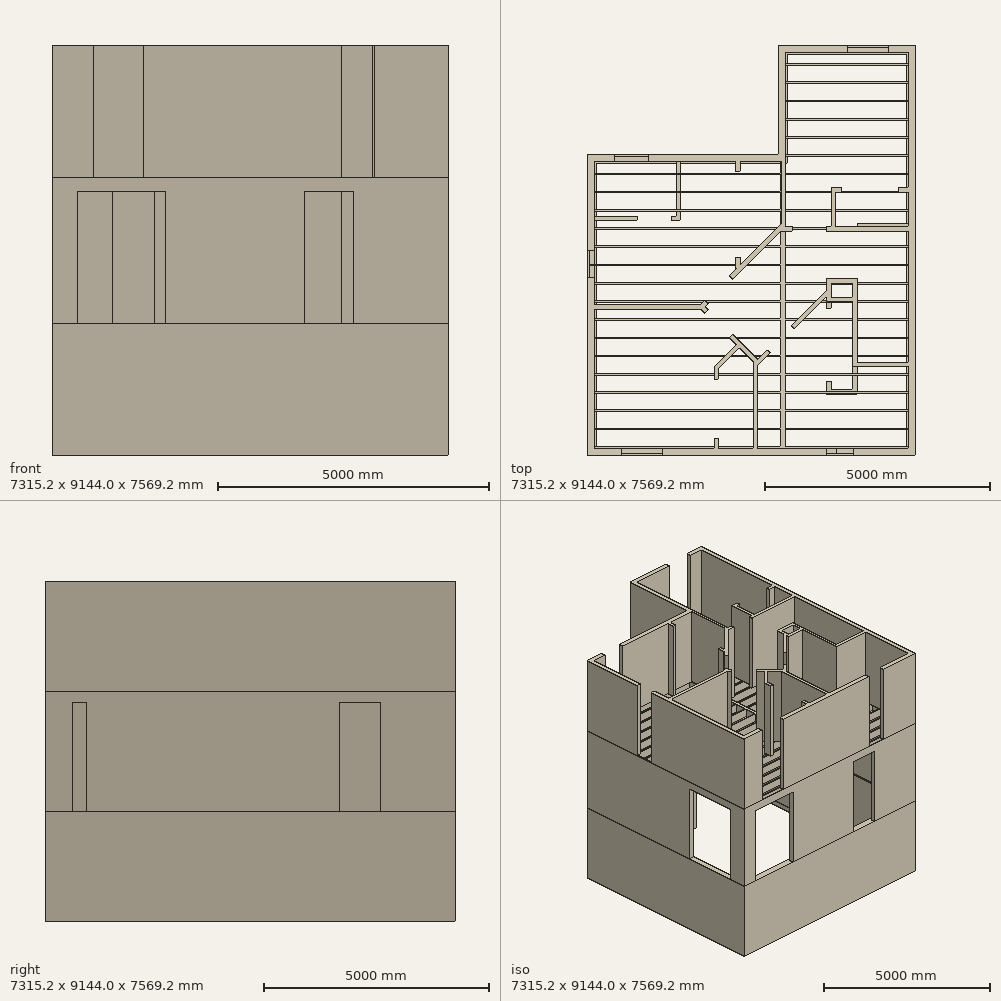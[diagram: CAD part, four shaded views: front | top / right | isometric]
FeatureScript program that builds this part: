
annotation { "Feature Type Name" : "Feature", "Feature Type Description" : "" }
export const myFeature = defineFeature(function(context is Context, id is Id, definition is map)
    precondition{}
    {
        {
            var Q0;
            Q0=qCreatedBy(makeId("Top.planeOp"),FACE);
            cPlane(context, id + "F0", {"entities" : qUnion([Q0]), "cplaneType" : CPlaneType.OFFSET, "offset" : 2692.4 * mm, "width" : 152.4 * mm, "height" : 152.4 * mm});
        }
        {
            var Q0;
            Q0=qCreatedBy(makeId("Top.planeOp"),FACE);
            var sketch = newSketch(context, id + "F1", { "sketchPlane" : qUnion([Q0])});
            skLineSegment(sketch, "E0", {"start": v(-4267.2, 6705.6) * mm, "end": v(0, 6705.6) * mm});
            skLineSegment(sketch, "E1", {"start": v(0, 9144) * mm, "end": v(0, 6705.6) * mm});
            skLineSegment(sketch, "E2", {"start": v(0, 9144) * mm, "end": v(3048, 9144) * mm});
            skLineSegment(sketch, "E3", {"start": v(3048, 9144) * mm, "end": v(3048, 0) * mm});
            skLineSegment(sketch, "E4", {"start": v(3048, 0) * mm, "end": v(-4267.2, 0) * mm});
            skLineSegment(sketch, "E5", {"start": v(-4267.2, 0) * mm, "end": v(-4267.2, 6705.6) * mm});
            skLineSegment(sketch, "E6", {"start": v(-4267.2, 6705.6) * mm, "end": v(-4267.2, 10363.2) * mm});
            skLineSegment(sketch, "E7", {"start": v(-3048, 11582.4) * mm, "end": v(3048, 11582.4) * mm});
            skLineSegment(sketch, "E8", {"start": v(3048, 11582.4) * mm, "end": v(3048, 9144) * mm});
            skLineSegment(sketch, "E9", {"start": v(-4267.2, 0) * mm, "end": v(-4267.2, -2743.2) * mm});
            skLineSegment(sketch, "E10", {"start": v(-4267.2, -2743.2) * mm, "end": v(3048, -2743.2) * mm});
            skLineSegment(sketch, "E11", {"start": v(3048, -2743.2) * mm, "end": v(3048, 0) * mm});
            skLineSegment(sketch, "E12", {"start": v(-4267.2, 10363.2) * mm, "end": v(-3048, 11582.4) * mm});
            skSolve(sketch);
        }
        {
            var Q0;
            Q0=qCreatedBy(makeId("Top.planeOp"),FACE);
            var sketch = newSketch(context, id + "F2", { "sketchPlane" : qUnion([Q0])});
            skLineSegment(sketch, "E13", {"start": v(0, 0) * mm, "end": v(-4267.2, 0) * mm});
            skLineSegment(sketch, "E14", {"start": v(-4267.2, 0) * mm, "end": v(-4267.2, 6705.6) * mm});
            skLineSegment(sketch, "E15", {"start": v(-4267.2, 6705.6) * mm, "end": v(0, 6705.6) * mm});
            skLineSegment(sketch, "E16", {"start": v(0, 6705.6) * mm, "end": v(0, 9144) * mm});
            skLineSegment(sketch, "E17", {"start": v(0, 9144) * mm, "end": v(3048, 9144) * mm});
            skLineSegment(sketch, "E18", {"start": v(3048, 9144) * mm, "end": v(3048, 0) * mm});
            skLineSegment(sketch, "E19", {"start": v(3048, 0) * mm, "end": v(0, 0) * mm});
            skLineSegment(sketch, "E20.0", {"start": v(203.2, 6502.4) * mm, "end": v(203.2, 8940.8) * mm});
            skLineSegment(sketch, "E20.1", {"start": v(-4064, 6502.4) * mm, "end": v(203.2, 6502.4) * mm});
            skLineSegment(sketch, "E20.2", {"start": v(2844.8, 8940.8) * mm, "end": v(2844.8, 203.2) * mm});
            skLineSegment(sketch, "E20.3", {"start": v(2844.8, 203.2) * mm, "end": v(0, 203.2) * mm});
            skLineSegment(sketch, "E20.4", {"start": v(0, 203.2) * mm, "end": v(-4064, 203.2) * mm});
            skLineSegment(sketch, "E20.5", {"start": v(203.2, 8940.8) * mm, "end": v(2844.8, 8940.8) * mm});
            skLineSegment(sketch, "E20.6", {"start": v(-4064, 203.2) * mm, "end": v(-4064, 6502.4) * mm});
            skSolve(sketch);
        }
        {
            var Q0;
            Q0 = qSketchRegion(id + "F2", true);
            extrude(context, id + "F3", {"entities" : qUnion([Q0]), "oppositeDirection" : true, "depth" : 2438.4 * mm});
        }
        {
            var Q0;
            Q0=makeQuery(id+"F1.imprint","IMPRINT",FACE,{"disambiguationData":[TD([[makeQuery(id+"F1.imprint","IMPRINT",EDGE,{"derivedFrom":sQuery(id+"F1.wireOp",EDGE,"E0")}),1.0]])]});
            var sketch = newSketch(context, id + "F4", { "sketchPlane" : qUnion([Q0])});
            skLineSegment(sketch, "E21.bottom", {"start": v(-4267.2, 0) * mm, "end": v(-3810, 0) * mm});
            skLineSegment(sketch, "E21.top", {"start": v(-4114.8, 152.4) * mm, "end": v(-3810, 152.4) * mm});
            skLineSegment(sketch, "E21.left", {"start": v(-4267.2, 0) * mm, "end": v(-4267.2, 152.4) * mm});
            skLineSegment(sketch, "E21.right", {"start": v(-3810, 0) * mm, "end": v(-3810, 152.4) * mm});
            skLineSegment(sketch, "E22.top", {"start": v(-4267.2, 609.6) * mm, "end": v(-4114.8, 609.6) * mm});
            skLineSegment(sketch, "E22.left", {"start": v(-4267.2, 152.4) * mm, "end": v(-4267.2, 609.6) * mm});
            skLineSegment(sketch, "E22.right", {"start": v(-4114.8, 152.4) * mm, "end": v(-4114.8, 609.6) * mm});
            skLineSegment(sketch, "E23.bottom", {"start": v(-4267.2, 2336.8) * mm, "end": v(-4114.8, 2336.8) * mm});
            skLineSegment(sketch, "E23.top", {"start": v(-4267.2, 6705.6) * mm, "end": v(-4114.8, 6705.6) * mm});
            skLineSegment(sketch, "E23.left", {"start": v(-4267.2, 2336.8) * mm, "end": v(-4267.2, 6705.6) * mm});
            skLineSegment(sketch, "E23.right", {"start": v(-4114.8, 2336.8) * mm, "end": v(-4114.8, 5232.4) * mm});
            skLineSegment(sketch, "E24.bottom", {"start": v(-4114.8, 6705.6) * mm, "end": v(-1879.6, 6705.6) * mm});
            skLineSegment(sketch, "E24.top", {"start": v(-4114.8, 6553.2) * mm, "end": v(-2286, 6553.2) * mm});
            skLineSegment(sketch, "E24.right", {"start": v(-1879.6, 6705.6) * mm, "end": v(-1879.6, 6553.2) * mm});
            skLineSegment(sketch, "E25.bottom", {"start": v(-1066.8, 6705.6) * mm, "end": v(0, 6705.6) * mm});
            skLineSegment(sketch, "E25.top", {"start": v(-1066.8, 6553.2) * mm, "end": v(0, 6553.2) * mm});
            skLineSegment(sketch, "E25.left", {"start": v(-1066.8, 6705.6) * mm, "end": v(-1066.8, 6553.2) * mm});
            skLineSegment(sketch, "E26.bottom", {"start": v(0, 6553.2) * mm, "end": v(152.4, 6553.2) * mm});
            skLineSegment(sketch, "E26.top", {"start": v(0, 9144) * mm, "end": v(152.4, 9144) * mm});
            skLineSegment(sketch, "E26.left", {"start": v(0, 6705.6) * mm, "end": v(0, 9144) * mm});
            skLineSegment(sketch, "E26.right", {"start": v(152.4, 6553.2) * mm, "end": v(152.4, 8991.6) * mm});
            skLineSegment(sketch, "E27.bottom", {"start": v(152.4, 9144) * mm, "end": v(3048, 9144) * mm});
            skLineSegment(sketch, "E27.top", {"start": v(152.4, 8991.6) * mm, "end": v(2895.6, 8991.6) * mm});
            skLineSegment(sketch, "E28.top", {"start": v(3048, 7467.6) * mm, "end": v(2895.6, 7467.6) * mm});
            skLineSegment(sketch, "E28.left", {"start": v(3048, 8991.6) * mm, "end": v(3048, 7467.6) * mm});
            skLineSegment(sketch, "E28.right", {"start": v(2895.6, 8991.6) * mm, "end": v(2895.6, 7467.6) * mm});
            skLineSegment(sketch, "E29.bottom", {"start": v(3048, 6553.2) * mm, "end": v(2895.6, 6553.2) * mm});
            skLineSegment(sketch, "E29.top", {"start": v(3048, 914.4) * mm, "end": v(2895.6, 914.4) * mm});
            skLineSegment(sketch, "E29.left", {"start": v(3048, 6553.2) * mm, "end": v(3048, 914.4) * mm});
            skLineSegment(sketch, "E29.right", {"start": v(2895.6, 6553.2) * mm, "end": v(2895.6, 5181.6) * mm});
            skLineSegment(sketch, "E30.bottom", {"start": v(-2184.4, 0) * mm, "end": v(381, 0) * mm});
            skLineSegment(sketch, "E30.top", {"start": v(-2184.4, 152.4) * mm, "end": v(50.8, 152.4) * mm});
            skLineSegment(sketch, "E30.left", {"start": v(-2184.4, 0) * mm, "end": v(-2184.4, 152.4) * mm});
            skLineSegment(sketch, "E31.bottom", {"start": v(1295.4, 152.4) * mm, "end": v(2895.6, 152.4) * mm});
            skLineSegment(sketch, "E31.top", {"start": v(1295.4, 0) * mm, "end": v(3048, 0) * mm});
            skLineSegment(sketch, "E31.left", {"start": v(1295.4, 152.4) * mm, "end": v(1295.4, 0) * mm});
            skLineSegment(sketch, "E31.right", {"start": v(3048, 152.4) * mm, "end": v(3048, 0) * mm});
            skLineSegment(sketch, "E32.top", {"start": v(3048, 609.6) * mm, "end": v(2895.6, 609.6) * mm});
            skLineSegment(sketch, "E32.left", {"start": v(3048, 152.4) * mm, "end": v(3048, 609.6) * mm});
            skLineSegment(sketch, "E32.right", {"start": v(2895.6, 152.4) * mm, "end": v(2895.6, 609.6) * mm});
            skLineSegment(sketch, "E33.bottom", {"start": v(-4114.8, 5334) * mm, "end": v(-3149.6, 5334) * mm});
            skLineSegment(sketch, "E33.top", {"start": v(-4114.8, 5232.4) * mm, "end": v(-3149.6, 5232.4) * mm});
            skLineSegment(sketch, "E33.right", {"start": v(-3149.6, 5334) * mm, "end": v(-3149.6, 5232.4) * mm});
            skLineSegment(sketch, "E34.bottom", {"start": v(-2387.6, 5334) * mm, "end": v(-2286, 5334) * mm});
            skLineSegment(sketch, "E34.top", {"start": v(-2387.6, 5232.4) * mm, "end": v(-2184.4, 5232.4) * mm});
            skLineSegment(sketch, "E34.left", {"start": v(-2387.6, 5334) * mm, "end": v(-2387.6, 5232.4) * mm});
            skLineSegment(sketch, "E34.right", {"start": v(-2184.4, 5334) * mm, "end": v(-2184.4, 5232.4) * mm});
            skLineSegment(sketch, "E35.left", {"start": v(-2184.4, 5334) * mm, "end": v(-2184.4, 6553.2) * mm});
            skLineSegment(sketch, "E35.right", {"start": v(-2286, 5334) * mm, "end": v(-2286, 6553.2) * mm});
            skLineSegment(sketch, "E36.bottom", {"start": v(381, 152.4) * mm, "end": v(152.4, 152.4) * mm});
            skLineSegment(sketch, "E36.top", {"start": v(152.4, 1066.8) * mm, "end": v(50.8, 1066.8) * mm});
            skLineSegment(sketch, "E36.left", {"start": v(152.4, 152.4) * mm, "end": v(152.4, 1066.8) * mm});
            skLineSegment(sketch, "E36.right", {"start": v(50.8, 152.4) * mm, "end": v(50.8, 1066.8) * mm});
            skLineSegment(sketch, "E37.bottom", {"start": v(50.8, 3937.1) * mm, "end": v(152.4, 3937.1) * mm});
            skLineSegment(sketch, "E37.top", {"start": v(50.8, 2286) * mm, "end": v(152.4, 2286) * mm});
            skLineSegment(sketch, "E37.left", {"start": v(50.8, 3937.1) * mm, "end": v(50.8, 2286) * mm});
            skLineSegment(sketch, "E37.right", {"start": v(152.4, 3937.1) * mm, "end": v(152.4, 2286) * mm});
            skLineSegment(sketch, "E38", {"start": v(1066.8, 3937.1) * mm, "end": v(1752.6, 3937.1) * mm});
            skLineSegment(sketch, "E39", {"start": v(1752.6, 3937.1) * mm, "end": v(1752.6, 1371.6) * mm});
            skLineSegment(sketch, "E40", {"start": v(1752.6, 1371.6) * mm, "end": v(1066.8, 1371.6) * mm});
            skLineSegment(sketch, "E41", {"start": v(1066.8, 1371.6) * mm, "end": v(1066.8, 1655.98) * mm});
            skLineSegment(sketch, "E42", {"start": v(1066.8, 3937.1) * mm, "end": v(1066.8, 3276.8) * mm});
            skLineSegment(sketch, "E43.0", {"start": v(1168.4, 3835.5) * mm, "end": v(1168.4, 3530.7) * mm});
            skLineSegment(sketch, "E43.1", {"start": v(1168.4, 1473.2) * mm, "end": v(1168.4, 1655.98) * mm});
            skLineSegment(sketch, "E43.2", {"start": v(1651, 1473.2) * mm, "end": v(1168.4, 1473.2) * mm});
            skLineSegment(sketch, "E43.3", {"start": v(1651, 3835.5) * mm, "end": v(1651, 3530.7) * mm});
            skLineSegment(sketch, "E43.4", {"start": v(1168.4, 3835.5) * mm, "end": v(1651, 3835.5) * mm});
            skLineSegment(sketch, "E44", {"start": v(1066.8, 1655.98) * mm, "end": v(1168.4, 1655.98) * mm});
            skLineSegment(sketch, "E45", {"start": v(1066.8, 3276.8) * mm, "end": v(1168.4, 3276.8) * mm});
            skLineSegment(sketch, "E46", {"start": v(1168.4, 3429.2) * mm, "end": v(1651, 3429.2) * mm});
            skLineSegment(sketch, "E47", {"start": v(1651, 3530.7) * mm, "end": v(1168.4, 3530.7) * mm});
            skLineSegment(sketch, "E48.trimOffspring", {"start": v(1168.4, 3429.2) * mm, "end": v(1168.4, 3276.8) * mm});
            skLineSegment(sketch, "E49.trimOffspring", {"start": v(1651, 3429.2) * mm, "end": v(1651, 1473.2) * mm});
            skPoint(sketch, "E50.orphan", {"position": v(152.4, 152.4) * mm});
            skLineSegment(sketch, "E51", {"start": v(381, 152.4) * mm, "end": v(381, 0) * mm});
            skLineSegment(sketch, "E52.trimOffspring", {"start": v(-2184.4, 6553.2) * mm, "end": v(-1879.6, 6553.2) * mm});
            skLineSegment(sketch, "E53.trimOffspring", {"start": v(-4114.8, 5334) * mm, "end": v(-4114.8, 6553.2) * mm});
            skLineSegment(sketch, "E54", {"start": v(3048, 9144) * mm, "end": v(3048, 8991.6) * mm});
            skLineSegment(sketch, "E55", {"start": v(2895.6, 5181.6) * mm, "end": v(1752.6, 5181.6) * mm});
            skLineSegment(sketch, "E56", {"start": v(1752.6, 5181.6) * mm, "end": v(1752.6, 5080.1) * mm});
            skLineSegment(sketch, "E57", {"start": v(1752.6, 5080.1) * mm, "end": v(2895.6, 5080.1) * mm});
            skLineSegment(sketch, "E58.trimOffspring", {"start": v(2895.6, 5080.1) * mm, "end": v(2895.6, 914.4) * mm});
            skSolve(sketch);
        }
        {
            var Q0;
            Q0 = qSketchRegion(id + "F4", true);
            extrude(context, id + "F5", {"entities" : qUnion([Q0]), "depth" : 2438.4 * mm});
        }
        {
            var Q0;
            Q0=qCreatedBy(makeId("Front.planeOp"),FACE);
            var sketch = newSketch(context, id + "F6", { "sketchPlane" : qUnion([Q0])});
            skLineSegment(sketch, "E59.bottom", {"start": v(152.4, 2692.4) * mm, "end": v(38.1, 2692.4) * mm});
            skLineSegment(sketch, "E59.top", {"start": v(152.4, 2438.4) * mm, "end": v(38.1, 2438.4) * mm});
            skLineSegment(sketch, "E59.left", {"start": v(152.4, 2692.4) * mm, "end": v(152.4, 2438.4) * mm});
            skLineSegment(sketch, "E59.right", {"start": v(38.1, 2692.4) * mm, "end": v(38.1, 2438.4) * mm});
            skPoint(sketch, "E60.firstSnap0", {"position": v(95.25, 2692.4) * mm});
            skLineSegment(sketch, "E60.bottom", {"start": v(3048, 2692.4) * mm, "end": v(3009.9, 2692.4) * mm});
            skLineSegment(sketch, "E60.top", {"start": v(3048, 2438.4) * mm, "end": v(3009.9, 2438.4) * mm});
            skLineSegment(sketch, "E60.left", {"start": v(3048, 2692.4) * mm, "end": v(3048, 2438.4) * mm});
            skLineSegment(sketch, "E60.right", {"start": v(3009.9, 2692.4) * mm, "end": v(3009.9, 2438.4) * mm});
            skLineSegment(sketch, "E61.bottom", {"start": v(-4229.1, 2692.4) * mm, "end": v(-4267.2, 2692.4) * mm});
            skLineSegment(sketch, "E61.top", {"start": v(-4229.1, 2438.4) * mm, "end": v(-4267.2, 2438.4) * mm});
            skLineSegment(sketch, "E61.left", {"start": v(-4229.1, 2692.4) * mm, "end": v(-4229.1, 2438.4) * mm});
            skLineSegment(sketch, "E61.right", {"start": v(-4267.2, 2692.4) * mm, "end": v(-4267.2, 2438.4) * mm});
            skSolve(sketch);
        }
        {
            var Q0;
            Q0 = qSketchRegion(id + "F6", true);
            var Q1;
            Q1=makeQuery(id+"F5.opExtrude","SWEPT_FACE",FACE,{"disambiguationData":[OSD([sQuery(id+"F4.wireOp",EDGE,"E26.top"),sQuery(id+"F4.wireOp",EDGE,"E27.bottom")])]});
            extrude(context, id + "F7", {"entities" : qUnion([Q0]), "oppositeDirection" : true, "depth" : 9144 * mm});
        }
        {
            var Q0;
            Q0=makeQuery(id+"F5.opExtrude","SWEPT_FACE",FACE,{"disambiguationData":[OSD([sQuery(id+"F4.wireOp",EDGE,"E23.left")])]});
            var sketch = newSketch(context, id + "F8", { "sketchPlane" : qUnion([Q0])});
            skLineSegment(sketch, "E62.bottom", {"start": v(-9144, 2692.4) * mm, "end": v(-9105.9, 2692.4) * mm});
            skLineSegment(sketch, "E62.top", {"start": v(-9144, 2438.4) * mm, "end": v(-9105.9, 2438.4) * mm});
            skLineSegment(sketch, "E62.left", {"start": v(-9144, 2692.4) * mm, "end": v(-9144, 2438.4) * mm});
            skLineSegment(sketch, "E62.right", {"start": v(-9105.9, 2692.4) * mm, "end": v(-9105.9, 2438.4) * mm});
            skLineSegment(sketch, "E63.1.0.0", {"start": v(-8737.6, 2438.4) * mm, "end": v(-8699.5, 2438.4) * mm});
            skLineSegment(sketch, "E63.1.0.1", {"start": v(-8737.6, 2692.4) * mm, "end": v(-8737.6, 2438.4) * mm});
            skLineSegment(sketch, "E63.1.0.2", {"start": v(-8699.5, 2692.4) * mm, "end": v(-8699.5, 2438.4) * mm});
            skLineSegment(sketch, "E63.1.0.3", {"start": v(-8737.6, 2692.4) * mm, "end": v(-8699.5, 2692.4) * mm});
            skLineSegment(sketch, "E63.2.0.0", {"start": v(-8331.2, 2438.4) * mm, "end": v(-8293.1, 2438.4) * mm});
            skLineSegment(sketch, "E63.2.0.1", {"start": v(-8331.2, 2692.4) * mm, "end": v(-8331.2, 2438.4) * mm});
            skLineSegment(sketch, "E63.2.0.2", {"start": v(-8293.1, 2692.4) * mm, "end": v(-8293.1, 2438.4) * mm});
            skLineSegment(sketch, "E63.2.0.3", {"start": v(-8331.2, 2692.4) * mm, "end": v(-8293.1, 2692.4) * mm});
            skLineSegment(sketch, "E63.3.0.0", {"start": v(-7924.8, 2438.4) * mm, "end": v(-7886.7, 2438.4) * mm});
            skLineSegment(sketch, "E63.3.0.1", {"start": v(-7924.8, 2692.4) * mm, "end": v(-7924.8, 2438.4) * mm});
            skLineSegment(sketch, "E63.3.0.2", {"start": v(-7886.7, 2692.4) * mm, "end": v(-7886.7, 2438.4) * mm});
            skLineSegment(sketch, "E63.3.0.3", {"start": v(-7924.8, 2692.4) * mm, "end": v(-7886.7, 2692.4) * mm});
            skLineSegment(sketch, "E63.4.0.0", {"start": v(-7518.4, 2438.4) * mm, "end": v(-7480.3, 2438.4) * mm});
            skLineSegment(sketch, "E63.4.0.1", {"start": v(-7518.4, 2692.4) * mm, "end": v(-7518.4, 2438.4) * mm});
            skLineSegment(sketch, "E63.4.0.2", {"start": v(-7480.3, 2692.4) * mm, "end": v(-7480.3, 2438.4) * mm});
            skLineSegment(sketch, "E63.4.0.3", {"start": v(-7518.4, 2692.4) * mm, "end": v(-7480.3, 2692.4) * mm});
            skLineSegment(sketch, "E63.5.0.0", {"start": v(-7112, 2438.4) * mm, "end": v(-7073.9, 2438.4) * mm});
            skLineSegment(sketch, "E63.5.0.1", {"start": v(-7112, 2692.4) * mm, "end": v(-7112, 2438.4) * mm});
            skLineSegment(sketch, "E63.5.0.2", {"start": v(-7073.9, 2692.4) * mm, "end": v(-7073.9, 2438.4) * mm});
            skLineSegment(sketch, "E63.5.0.3", {"start": v(-7112, 2692.4) * mm, "end": v(-7073.9, 2692.4) * mm});
            skLineSegment(sketch, "E63.6.0.0", {"start": v(-6705.6, 2438.4) * mm, "end": v(-6667.5, 2438.4) * mm});
            skLineSegment(sketch, "E63.6.0.1", {"start": v(-6705.6, 2692.4) * mm, "end": v(-6705.6, 2438.4) * mm});
            skLineSegment(sketch, "E63.6.0.2", {"start": v(-6667.5, 2692.4) * mm, "end": v(-6667.5, 2438.4) * mm});
            skLineSegment(sketch, "E63.6.0.3", {"start": v(-6705.6, 2692.4) * mm, "end": v(-6667.5, 2692.4) * mm});
            skLineSegment(sketch, "E63.7.0.0", {"start": v(-6299.2, 2438.4) * mm, "end": v(-6261.1, 2438.4) * mm});
            skLineSegment(sketch, "E63.7.0.1", {"start": v(-6299.2, 2692.4) * mm, "end": v(-6299.2, 2438.4) * mm});
            skLineSegment(sketch, "E63.7.0.2", {"start": v(-6261.1, 2692.4) * mm, "end": v(-6261.1, 2438.4) * mm});
            skLineSegment(sketch, "E63.7.0.3", {"start": v(-6299.2, 2692.4) * mm, "end": v(-6261.1, 2692.4) * mm});
            skLineSegment(sketch, "E63.8.0.0", {"start": v(-5892.8, 2438.4) * mm, "end": v(-5854.7, 2438.4) * mm});
            skLineSegment(sketch, "E63.8.0.1", {"start": v(-5892.8, 2692.4) * mm, "end": v(-5892.8, 2438.4) * mm});
            skLineSegment(sketch, "E63.8.0.2", {"start": v(-5854.7, 2692.4) * mm, "end": v(-5854.7, 2438.4) * mm});
            skLineSegment(sketch, "E63.8.0.3", {"start": v(-5892.8, 2692.4) * mm, "end": v(-5854.7, 2692.4) * mm});
            skLineSegment(sketch, "E63.9.0.0", {"start": v(-5486.4, 2438.4) * mm, "end": v(-5448.3, 2438.4) * mm});
            skLineSegment(sketch, "E63.9.0.1", {"start": v(-5486.4, 2692.4) * mm, "end": v(-5486.4, 2438.4) * mm});
            skLineSegment(sketch, "E63.9.0.2", {"start": v(-5448.3, 2692.4) * mm, "end": v(-5448.3, 2438.4) * mm});
            skLineSegment(sketch, "E63.9.0.3", {"start": v(-5486.4, 2692.4) * mm, "end": v(-5448.3, 2692.4) * mm});
            skLineSegment(sketch, "E63.10.0.0", {"start": v(-5080, 2438.4) * mm, "end": v(-5041.9, 2438.4) * mm});
            skLineSegment(sketch, "E63.10.0.1", {"start": v(-5080, 2692.4) * mm, "end": v(-5080, 2438.4) * mm});
            skLineSegment(sketch, "E63.10.0.2", {"start": v(-5041.9, 2692.4) * mm, "end": v(-5041.9, 2438.4) * mm});
            skLineSegment(sketch, "E63.10.0.3", {"start": v(-5080, 2692.4) * mm, "end": v(-5041.9, 2692.4) * mm});
            skLineSegment(sketch, "E63.11.0.0", {"start": v(-4673.6, 2438.4) * mm, "end": v(-4635.5, 2438.4) * mm});
            skLineSegment(sketch, "E63.11.0.1", {"start": v(-4673.6, 2692.4) * mm, "end": v(-4673.6, 2438.4) * mm});
            skLineSegment(sketch, "E63.11.0.2", {"start": v(-4635.5, 2692.4) * mm, "end": v(-4635.5, 2438.4) * mm});
            skLineSegment(sketch, "E63.11.0.3", {"start": v(-4673.6, 2692.4) * mm, "end": v(-4635.5, 2692.4) * mm});
            skLineSegment(sketch, "E63.12.0.0", {"start": v(-4267.2, 2438.4) * mm, "end": v(-4229.1, 2438.4) * mm});
            skLineSegment(sketch, "E63.12.0.1", {"start": v(-4267.2, 2692.4) * mm, "end": v(-4267.2, 2438.4) * mm});
            skLineSegment(sketch, "E63.12.0.2", {"start": v(-4229.1, 2692.4) * mm, "end": v(-4229.1, 2438.4) * mm});
            skLineSegment(sketch, "E63.12.0.3", {"start": v(-4267.2, 2692.4) * mm, "end": v(-4229.1, 2692.4) * mm});
            skLineSegment(sketch, "E63.13.0.0", {"start": v(-3860.8, 2438.4) * mm, "end": v(-3822.7, 2438.4) * mm});
            skLineSegment(sketch, "E63.13.0.1", {"start": v(-3860.8, 2692.4) * mm, "end": v(-3860.8, 2438.4) * mm});
            skLineSegment(sketch, "E63.13.0.2", {"start": v(-3822.7, 2692.4) * mm, "end": v(-3822.7, 2438.4) * mm});
            skLineSegment(sketch, "E63.13.0.3", {"start": v(-3860.8, 2692.4) * mm, "end": v(-3822.7, 2692.4) * mm});
            skLineSegment(sketch, "E63.14.0.0", {"start": v(-3454.4, 2438.4) * mm, "end": v(-3416.3, 2438.4) * mm});
            skLineSegment(sketch, "E63.14.0.1", {"start": v(-3454.4, 2692.4) * mm, "end": v(-3454.4, 2438.4) * mm});
            skLineSegment(sketch, "E63.14.0.2", {"start": v(-3416.3, 2692.4) * mm, "end": v(-3416.3, 2438.4) * mm});
            skLineSegment(sketch, "E63.14.0.3", {"start": v(-3454.4, 2692.4) * mm, "end": v(-3416.3, 2692.4) * mm});
            skLineSegment(sketch, "E63.15.0.0", {"start": v(-3048, 2438.4) * mm, "end": v(-3009.9, 2438.4) * mm});
            skLineSegment(sketch, "E63.15.0.1", {"start": v(-3048, 2692.4) * mm, "end": v(-3048, 2438.4) * mm});
            skLineSegment(sketch, "E63.15.0.2", {"start": v(-3009.9, 2692.4) * mm, "end": v(-3009.9, 2438.4) * mm});
            skLineSegment(sketch, "E63.15.0.3", {"start": v(-3048, 2692.4) * mm, "end": v(-3009.9, 2692.4) * mm});
            skLineSegment(sketch, "E63.16.0.0", {"start": v(-2641.6, 2438.4) * mm, "end": v(-2603.5, 2438.4) * mm});
            skLineSegment(sketch, "E63.16.0.1", {"start": v(-2641.6, 2692.4) * mm, "end": v(-2641.6, 2438.4) * mm});
            skLineSegment(sketch, "E63.16.0.2", {"start": v(-2603.5, 2692.4) * mm, "end": v(-2603.5, 2438.4) * mm});
            skLineSegment(sketch, "E63.16.0.3", {"start": v(-2641.6, 2692.4) * mm, "end": v(-2603.5, 2692.4) * mm});
            skLineSegment(sketch, "E63.17.0.0", {"start": v(-2235.2, 2438.4) * mm, "end": v(-2197.1, 2438.4) * mm});
            skLineSegment(sketch, "E63.17.0.1", {"start": v(-2235.2, 2692.4) * mm, "end": v(-2235.2, 2438.4) * mm});
            skLineSegment(sketch, "E63.17.0.2", {"start": v(-2197.1, 2692.4) * mm, "end": v(-2197.1, 2438.4) * mm});
            skLineSegment(sketch, "E63.17.0.3", {"start": v(-2235.2, 2692.4) * mm, "end": v(-2197.1, 2692.4) * mm});
            skLineSegment(sketch, "E63.18.0.0", {"start": v(-1828.8, 2438.4) * mm, "end": v(-1790.7, 2438.4) * mm});
            skLineSegment(sketch, "E63.18.0.1", {"start": v(-1828.8, 2692.4) * mm, "end": v(-1828.8, 2438.4) * mm});
            skLineSegment(sketch, "E63.18.0.2", {"start": v(-1790.7, 2692.4) * mm, "end": v(-1790.7, 2438.4) * mm});
            skLineSegment(sketch, "E63.18.0.3", {"start": v(-1828.8, 2692.4) * mm, "end": v(-1790.7, 2692.4) * mm});
            skLineSegment(sketch, "E63.19.0.0", {"start": v(-1422.4, 2438.4) * mm, "end": v(-1384.3, 2438.4) * mm});
            skLineSegment(sketch, "E63.19.0.1", {"start": v(-1422.4, 2692.4) * mm, "end": v(-1422.4, 2438.4) * mm});
            skLineSegment(sketch, "E63.19.0.2", {"start": v(-1384.3, 2692.4) * mm, "end": v(-1384.3, 2438.4) * mm});
            skLineSegment(sketch, "E63.19.0.3", {"start": v(-1422.4, 2692.4) * mm, "end": v(-1384.3, 2692.4) * mm});
            skLineSegment(sketch, "E63.20.0.0", {"start": v(-1016, 2438.4) * mm, "end": v(-977.9, 2438.4) * mm});
            skLineSegment(sketch, "E63.20.0.1", {"start": v(-1016, 2692.4) * mm, "end": v(-1016, 2438.4) * mm});
            skLineSegment(sketch, "E63.20.0.2", {"start": v(-977.9, 2692.4) * mm, "end": v(-977.9, 2438.4) * mm});
            skLineSegment(sketch, "E63.20.0.3", {"start": v(-1016, 2692.4) * mm, "end": v(-977.9, 2692.4) * mm});
            skLineSegment(sketch, "E63.21.0.0", {"start": v(-609.6, 2438.4) * mm, "end": v(-571.5, 2438.4) * mm});
            skLineSegment(sketch, "E63.21.0.1", {"start": v(-609.6, 2692.4) * mm, "end": v(-609.6, 2438.4) * mm});
            skLineSegment(sketch, "E63.21.0.2", {"start": v(-571.5, 2692.4) * mm, "end": v(-571.5, 2438.4) * mm});
            skLineSegment(sketch, "E63.21.0.3", {"start": v(-609.6, 2692.4) * mm, "end": v(-571.5, 2692.4) * mm});
            skLineSegment(sketch, "E63.22.0.0", {"start": v(-203.2, 2438.4) * mm, "end": v(-165.1, 2438.4) * mm});
            skLineSegment(sketch, "E63.22.0.1", {"start": v(-203.2, 2692.4) * mm, "end": v(-203.2, 2438.4) * mm});
            skLineSegment(sketch, "E63.22.0.2", {"start": v(-165.1, 2692.4) * mm, "end": v(-165.1, 2438.4) * mm});
            skLineSegment(sketch, "E63.22.0.3", {"start": v(-203.2, 2692.4) * mm, "end": v(-165.1, 2692.4) * mm});
            skLineSegment(sketch, "E63.direction1", {"start": v(-9144, 2438.4) * mm, "end": v(-8737.6, 2438.4) * mm, "construction": true});
            skLineSegment(sketch, "E64.bottom", {"start": v(-38.1, 2692.4) * mm, "end": v(0, 2692.4) * mm});
            skLineSegment(sketch, "E64.top", {"start": v(-38.1, 2438.4) * mm, "end": v(0, 2438.4) * mm});
            skLineSegment(sketch, "E64.left", {"start": v(-38.1, 2692.4) * mm, "end": v(-38.1, 2438.4) * mm});
            skLineSegment(sketch, "E64.right", {"start": v(0, 2692.4) * mm, "end": v(0, 2438.4) * mm});
            skSolve(sketch);
        }
        {
            var Q0;
            Q0 = qSketchRegion(id + "F8", true);
            extrude(context, id + "F9", {"entities" : qUnion([Q0]), "operationType" : NewBodyOperationType.ADD, "oppositeDirection" : true, "depth" : 7315.2 * mm});
        }
        {
            var Q0;
            Q0=qCreatedBy(id+"F0.planeOp",FACE);
            var sketch = newSketch(context, id + "F10", { "sketchPlane" : qUnion([Q0])});
            skLineSegment(sketch, "E65", {"start": v(-4114.8, 6553.2) * mm, "end": v(-3657.6, 6553.2) * mm});
            skLineSegment(sketch, "E66", {"start": v(-3657.6, 6553.2) * mm, "end": v(-3657.6, 6705.6) * mm});
            skLineSegment(sketch, "E67", {"start": v(-3657.6, 6705.6) * mm, "end": v(-4267.2, 6705.6) * mm});
            skLineSegment(sketch, "E68", {"start": v(-4267.2, 6705.6) * mm, "end": v(-4267.2, 4582.06) * mm});
            skLineSegment(sketch, "E69", {"start": v(-4267.2, 4582.06) * mm, "end": v(-4114.8, 4582.06) * mm});
            skLineSegment(sketch, "E70", {"start": v(-4114.8, 4582.06) * mm, "end": v(-4114.8, 6553.2) * mm});
            skLineSegment(sketch, "E71", {"start": v(-4114.8, 3972.46) * mm, "end": v(-4114.8, 3362.86) * mm});
            skLineSegment(sketch, "E72", {"start": v(-4114.8, 3362.86) * mm, "end": v(-1733.68, 3362.86) * mm});
            skLineSegment(sketch, "E73", {"start": v(-1733.68, 3362.86) * mm, "end": v(-1640.9, 3455.65) * mm});
            skLineSegment(sketch, "E74", {"start": v(-1640.9, 3455.65) * mm, "end": v(-1569.12, 3383.88) * mm});
            skLineSegment(sketch, "E75", {"start": v(-1569.12, 3383.88) * mm, "end": v(-1640.9, 3312.1) * mm});
            skLineSegment(sketch, "E76", {"start": v(-1640.9, 3312.1) * mm, "end": v(-1569.12, 3240.34) * mm});
            skLineSegment(sketch, "E77", {"start": v(-1569.12, 3240.34) * mm, "end": v(-1640.9, 3168.57) * mm});
            skLineSegment(sketch, "E78", {"start": v(-1640.9, 3168.57) * mm, "end": v(-1733.68, 3261.36) * mm});
            skLineSegment(sketch, "E79", {"start": v(-1733.68, 3261.36) * mm, "end": v(-4114.8, 3261.36) * mm});
            skLineSegment(sketch, "E80", {"start": v(-4114.8, 3261.36) * mm, "end": v(-4114.8, 152.4) * mm});
            skLineSegment(sketch, "E81", {"start": v(-4114.8, 152.4) * mm, "end": v(-3505.2, 152.4) * mm});
            skLineSegment(sketch, "E82", {"start": v(-3505.2, 152.4) * mm, "end": v(-3505.2, 0) * mm});
            skLineSegment(sketch, "E83", {"start": v(-3505.2, 0) * mm, "end": v(-4267.2, 0) * mm});
            skLineSegment(sketch, "E84", {"start": v(-4267.2, 0) * mm, "end": v(-4267.2, 3972.46) * mm});
            skLineSegment(sketch, "E85", {"start": v(-4267.2, 3972.46) * mm, "end": v(-4114.8, 3972.46) * mm});
            skLineSegment(sketch, "E86", {"start": v(-2590.8, 152.4) * mm, "end": v(-1437.56, 152.4) * mm});
            skLineSegment(sketch, "E87", {"start": v(1066.8, 152.4) * mm, "end": v(1066.8, 0) * mm});
            skLineSegment(sketch, "E88", {"start": v(1066.8, 0) * mm, "end": v(-2590.8, 0) * mm});
            skLineSegment(sketch, "E89", {"start": v(-2590.8, 0) * mm, "end": v(-2590.8, 152.4) * mm});
            skLineSegment(sketch, "E90", {"start": v(-2590.8, 152.4) * mm, "end": v(-2590.8, 152.4) * mm});
            skLineSegment(sketch, "E91", {"start": v(1676.4, 152.4) * mm, "end": v(1676.4, 0) * mm});
            skLineSegment(sketch, "E92", {"start": v(1676.4, 0) * mm, "end": v(3048, 0) * mm});
            skLineSegment(sketch, "E93", {"start": v(3048, 0) * mm, "end": v(3048, 2081.78) * mm});
            skLineSegment(sketch, "E94", {"start": v(2895.6, 2081.78) * mm, "end": v(1752.6, 2081.78) * mm});
            skLineSegment(sketch, "E95", {"start": v(1752.6, 2081.78) * mm, "end": v(1752.6, 3937.1) * mm});
            skLineSegment(sketch, "E96", {"start": v(1752.6, 3937.1) * mm, "end": v(1066.8, 3937.1) * mm});
            skLineSegment(sketch, "E97", {"start": v(1066.8, 3937.1) * mm, "end": v(1066.8, 3683.15) * mm});
            skLineSegment(sketch, "E98", {"start": v(1066.8, 3429.2) * mm, "end": v(1652.02, 3429.2) * mm});
            skLineSegment(sketch, "E99", {"start": v(1652.02, 3429.2) * mm, "end": v(1652.02, 1981.2) * mm});
            skLineSegment(sketch, "E100", {"start": v(1652.02, 1981.2) * mm, "end": v(2895.6, 1981.2) * mm});
            skLineSegment(sketch, "E101", {"start": v(2895.6, 1981.2) * mm, "end": v(2895.6, 152.4) * mm});
            skLineSegment(sketch, "E102", {"start": v(2895.6, 152.4) * mm, "end": v(1676.4, 152.4) * mm});
            skLineSegment(sketch, "E103.bottom", {"start": v(1168.4, 3835.5) * mm, "end": v(1651, 3835.5) * mm});
            skLineSegment(sketch, "E103.top", {"start": v(1168.4, 3530.7) * mm, "end": v(1651, 3530.7) * mm});
            skLineSegment(sketch, "E103.left", {"start": v(1168.4, 3835.5) * mm, "end": v(1168.4, 3530.7) * mm});
            skLineSegment(sketch, "E103.right", {"start": v(1651, 3835.5) * mm, "end": v(1651, 3530.7) * mm});
            skLineSegment(sketch, "E104", {"start": v(-2895.6, 6705.6) * mm, "end": v(-2895.6, 6553.2) * mm});
            skLineSegment(sketch, "E105", {"start": v(-2895.6, 6553.2) * mm, "end": v(-965, 6553.2) * mm});
            skLineSegment(sketch, "E106", {"start": v(-965, 6553.2) * mm, "end": v(-965, 6324.6) * mm});
            skLineSegment(sketch, "E107", {"start": v(-965, 6324.6) * mm, "end": v(-863.5, 6324.6) * mm});
            skLineSegment(sketch, "E108", {"start": v(-863.5, 6324.6) * mm, "end": v(-863.5, 6553.2) * mm});
            skLineSegment(sketch, "E109", {"start": v(-863.5, 6553.2) * mm, "end": v(50.9, 6553.2) * mm});
            skLineSegment(sketch, "E110", {"start": v(50.9, 6553.2) * mm, "end": v(50.9, 5147.44) * mm});
            skLineSegment(sketch, "E111", {"start": v(50.88, 5003.88) * mm, "end": v(50.88, 5003.88) * mm});
            skLineSegment(sketch, "E112", {"start": v(152.4, 5105.4) * mm, "end": v(152.4, 6705.6) * mm});
            skLineSegment(sketch, "E113", {"start": v(0, 6705.6) * mm, "end": v(-2895.6, 6705.6) * mm});
            skLineSegment(sketch, "E114.top", {"start": v(-574.07, 152.4) * mm, "end": v(-472.57, 152.4) * mm});
            skLineSegment(sketch, "E114.left", {"start": v(-574.07, 2101.74) * mm, "end": v(-574.07, 152.4) * mm});
            skLineSegment(sketch, "E114.right", {"start": v(-472.57, 2000.24) * mm, "end": v(-472.57, 152.4) * mm});
            skLineSegment(sketch, "E115.top", {"start": v(-1640.9, 3312.1) * mm, "end": v(-472.57, 2143.79) * mm});
            skLineSegment(sketch, "E115.left", {"start": v(152.4, 5105.4) * mm, "end": v(-1640.9, 3312.1) * mm, "construction": true});
            skLineSegment(sketch, "E115.right", {"start": v(1066.8, 3683.15) * mm, "end": v(281.77, 2898.13) * mm});
            skLineSegment(sketch, "E116", {"start": v(-574.07, 2101.74) * mm, "end": v(-868.66, 2396.34) * mm});
            skLineSegment(sketch, "E117", {"start": v(-1102.08, 2629.75) * mm, "end": v(-1030.3, 2701.52) * mm});
            skLineSegment(sketch, "E118.0", {"start": v(1066.8, 3539.61) * mm, "end": v(353.54, 2826.36) * mm});
            skPoint(sketch, "E119.orphan", {"position": v(-472.57, 2143.79) * mm});
            skLineSegment(sketch, "E120", {"start": v(0, 6705.6) * mm, "end": v(0, 9144) * mm});
            skLineSegment(sketch, "E121", {"start": v(0, 9144) * mm, "end": v(1524, 9144) * mm});
            skLineSegment(sketch, "E122", {"start": v(1524, 9144) * mm, "end": v(1524, 8991.6) * mm});
            skLineSegment(sketch, "E123", {"start": v(1524, 8991.6) * mm, "end": v(152.4, 8991.6) * mm});
            skLineSegment(sketch, "E124", {"start": v(152.4, 8991.6) * mm, "end": v(152.4, 6705.6) * mm});
            skLineSegment(sketch, "E125", {"start": v(2438.4, 9144) * mm, "end": v(2438.4, 8991.6) * mm});
            skLineSegment(sketch, "E126", {"start": v(2438.4, 8991.6) * mm, "end": v(2895.6, 8991.6) * mm});
            skLineSegment(sketch, "E127", {"start": v(2895.6, 8991.6) * mm, "end": v(2895.6, 5968.9) * mm});
            skLineSegment(sketch, "E128", {"start": v(2895.6, 5105.4) * mm, "end": v(1269.8, 5105.4) * mm});
            skLineSegment(sketch, "E129", {"start": v(1066.8, 5105.4) * mm, "end": v(1066.8, 5003.9) * mm});
            skLineSegment(sketch, "E130", {"start": v(50.9, 5003.9) * mm, "end": v(304.8, 5003.9) * mm});
            skLineSegment(sketch, "E131", {"start": v(3048, 5003.9) * mm, "end": v(3048, 9144) * mm});
            skLineSegment(sketch, "E132", {"start": v(3048, 9144) * mm, "end": v(2438.4, 9144) * mm});
            skLineSegment(sketch, "E133", {"start": v(3048, 2081.78) * mm, "end": v(3048, 6420.6) * mm});
            skLineSegment(sketch, "E134", {"start": v(2895.6, 6420.6) * mm, "end": v(2895.6, 5968.9) * mm});
            skLineSegment(sketch, "E135", {"start": v(304.8, 5003.9) * mm, "end": v(304.8, 5105.4) * mm});
            skLineSegment(sketch, "E136.trimOffspring", {"start": v(1066.8, 5003.9) * mm, "end": v(2895.6, 5003.9) * mm});
            skLineSegment(sketch, "E137.trimOffspring", {"start": v(304.8, 5105.4) * mm, "end": v(152.4, 5105.4) * mm});
            skLineSegment(sketch, "E138.trimOffspring", {"start": v(2895.6, 5003.9) * mm, "end": v(2895.6, 2081.78) * mm});
            skLineSegment(sketch, "E139.trimOffspring", {"start": v(1066.8, 3539.61) * mm, "end": v(1066.8, 3429.2) * mm});
            skLineSegment(sketch, "E140", {"start": v(50.9, 5147.44) * mm, "end": v(-1102.08, 3994.46) * mm});
            skLineSegment(sketch, "E141", {"start": v(-1102.08, 3994.46) * mm, "end": v(-1030.3, 3922.7) * mm});
            skLineSegment(sketch, "E142", {"start": v(-1030.3, 3922.7) * mm, "end": v(50.9, 5003.9) * mm});
            skLineSegment(sketch, "E143", {"start": v(1168.3, 5105.4) * mm, "end": v(1168.3, 5968.9) * mm});
            skLineSegment(sketch, "E144", {"start": v(1168.3, 5968.9) * mm, "end": v(1396.9, 5968.9) * mm});
            skLineSegment(sketch, "E145", {"start": v(1396.9, 5968.9) * mm, "end": v(1396.9, 5867.4) * mm});
            skLineSegment(sketch, "E146", {"start": v(2895.6, 5867.4) * mm, "end": v(2667, 5867.4) * mm});
            skLineSegment(sketch, "E147", {"start": v(1269.8, 5867.4) * mm, "end": v(1269.8, 5105.4) * mm});
            skLineSegment(sketch, "E148.trimOffspring", {"start": v(1168.3, 5105.4) * mm, "end": v(1066.8, 5105.4) * mm});
            skLineSegment(sketch, "E149", {"start": v(2667, 5968.9) * mm, "end": v(2667, 5867.4) * mm});
            skLineSegment(sketch, "E150.trimOffspring", {"start": v(1396.9, 5867.4) * mm, "end": v(1269.8, 5867.4) * mm});
            skLineSegment(sketch, "E151.trimOffspring", {"start": v(2667, 5968.9) * mm, "end": v(2895.6, 5968.9) * mm});
            skLineSegment(sketch, "E152.trimOffspring", {"start": v(2895.6, 5867.4) * mm, "end": v(2895.6, 5105.4) * mm});
            skLineSegment(sketch, "E153", {"start": v(-940.43, 4156.1) * mm, "end": v(-965, 4180.68) * mm});
            skLineSegment(sketch, "E154", {"start": v(-965, 4180.68) * mm, "end": v(-965, 4409.28) * mm});
            skLineSegment(sketch, "E155", {"start": v(-965, 4409.28) * mm, "end": v(-863.5, 4409.28) * mm});
            skLineSegment(sketch, "E156", {"start": v(-863.5, 4409.28) * mm, "end": v(-863.5, 4222.72) * mm});
            skLineSegment(sketch, "E157", {"start": v(-868.66, 4227.88) * mm, "end": v(-863.5, 4222.72) * mm});
            skLineSegment(sketch, "E158", {"start": v(-257.04, 2359.31) * mm, "end": v(-185.27, 2287.54) * mm});
            skLineSegment(sketch, "E159", {"start": v(281.77, 2898.13) * mm, "end": v(353.54, 2826.36) * mm});
            skLineSegment(sketch, "E160.trimOffspring", {"start": v(-185.27, 2287.54) * mm, "end": v(-472.57, 2000.24) * mm});
            skLineSegment(sketch, "E161.trimOffspring", {"start": v(-257.04, 2359.31) * mm, "end": v(-472.57, 2143.79) * mm});
            skLineSegment(sketch, "E162", {"start": v(-1437.56, 152.4) * mm, "end": v(-1437.56, 381) * mm});
            skLineSegment(sketch, "E163", {"start": v(-1437.56, 381) * mm, "end": v(-1336.07, 381) * mm});
            skLineSegment(sketch, "E164", {"start": v(-1336.07, 381) * mm, "end": v(-1336.07, 152.4) * mm});
            skLineSegment(sketch, "E165", {"start": v(-940.43, 2468.1) * mm, "end": v(-1437.56, 1970.98) * mm});
            skLineSegment(sketch, "E166", {"start": v(-1437.56, 1970.98) * mm, "end": v(-1437.56, 1700.33) * mm});
            skLineSegment(sketch, "E167", {"start": v(-1437.56, 1700.33) * mm, "end": v(-1336.07, 1700.33) * mm});
            skLineSegment(sketch, "E168", {"start": v(-1336.07, 1700.33) * mm, "end": v(-1336.07, 1928.93) * mm});
            skLineSegment(sketch, "E169", {"start": v(-1336.07, 1928.93) * mm, "end": v(-868.66, 2396.34) * mm});
            skLineSegment(sketch, "E170.trimOffspring", {"start": v(-1336.07, 152.4) * mm, "end": v(1066.8, 152.4) * mm});
            skLineSegment(sketch, "E171.trimOffspring", {"start": v(-940.43, 2468.1) * mm, "end": v(-1102.08, 2629.75) * mm});
            skSolve(sketch);
        }
        {
            var Q0;
            Q0 = qSketchRegion(id + "F10", true);
            extrude(context, id + "F11", {"entities" : qUnion([Q0]), "depth" : 2438.4 * mm});
        }
        {
            var Q0;
            Q0=qCreatedBy(makeId("Top.planeOp"),FACE);
            var sketch = newSketch(context, id + "F12", { "sketchPlane" : qUnion([Q0])});
            skLineSegment(sketch, "E172.bottom", {"start": v(-4267.2, 0) * mm, "end": v(3048, 0) * mm});
            skLineSegment(sketch, "E172.top", {"start": v(0, 9144) * mm, "end": v(3048, 9144) * mm});
            skLineSegment(sketch, "E172.left", {"start": v(-4267.2, 0) * mm, "end": v(-4267.2, 6705.6) * mm});
            skLineSegment(sketch, "E172.right", {"start": v(3048, 0) * mm, "end": v(3048, 9144) * mm});
            skLineSegment(sketch, "E173", {"start": v(-4267.2, 6705.6) * mm, "end": v(0, 6705.6) * mm});
            skLineSegment(sketch, "E174", {"start": v(0, 6705.6) * mm, "end": v(0, 9144) * mm});
            skLineSegment(sketch, "E175.0", {"start": v(-8839.2, -4572) * mm, "end": v(-8839.2, 11277.6) * mm});
            skLineSegment(sketch, "E175.1", {"start": v(7620, -4572) * mm, "end": v(7620, 13716) * mm});
            skLineSegment(sketch, "E175.2", {"start": v(-4572, 13716) * mm, "end": v(7620, 13716) * mm});
            skLineSegment(sketch, "E175.3", {"start": v(-8839.2, -4572) * mm, "end": v(7620, -4572) * mm});
            skLineSegment(sketch, "E175.4", {"start": v(-4572, 11277.6) * mm, "end": v(-4572, 13716) * mm});
            skLineSegment(sketch, "E175.5", {"start": v(-8839.2, 11277.6) * mm, "end": v(-4572, 11277.6) * mm});
            skSolve(sketch);
        }
        {
            var Q0;
            Q0 = qSketchRegion(id + "F12", true);
            extrude(context, id + "F13", {"entities" : qUnion([Q0]), "operationType" : NewBodyOperationType.REMOVE, "endBound" : BoundingType.THROUGH_ALL, "depth" : 30.48 * mm});
        }
    });
